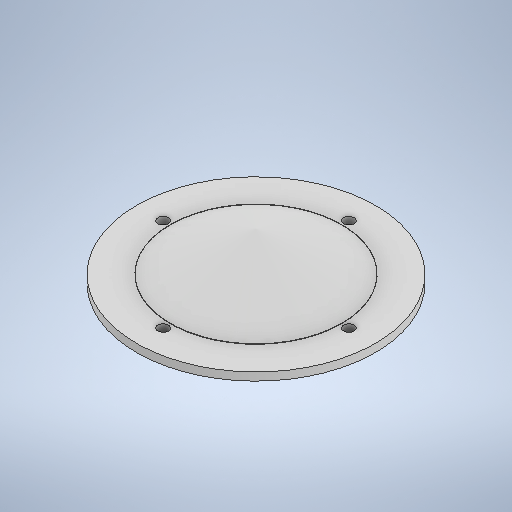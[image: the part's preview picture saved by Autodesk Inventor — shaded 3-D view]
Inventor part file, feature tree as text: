
AUTODESK INVENTOR PART (.ipt)
format: ipt  version: 2025 (Build 290162000, 162)  size: 284,672 bytes
history: native  units: mm
features: sketch x6, extrude x4, other x1, chamfer x1
ambient origin geometry x8: Origin, YZ Plane, XZ Plane, XY Plane, X Axis, Y Axis, Z Axis, Center Point
bodies: Body1 (feature_tree)
feature tree (12):
  other  "Bryła1"
  extrude  "Wyciągnięcie proste1"  Depth=90.0mm
  extrude  "Wyciągnięcie proste5"  Depth=3.0mm TaperAngle=0.0deg
  sketch  "Szkic8"
  extrude  "Wyciągnięcie proste9"  Depth=10.0mm
  sketch  "Szkic19"
  extrude  "Wyciągnięcie proste11"  Depth=2.0mm TaperAngle=0.0deg
  chamfer  "Faza1"  Distance=3.0mm
  sketch  "Szkic1"
  sketch  "Szkic4"
  sketch  "Szkic17"
  sketch  "Szkic20"
